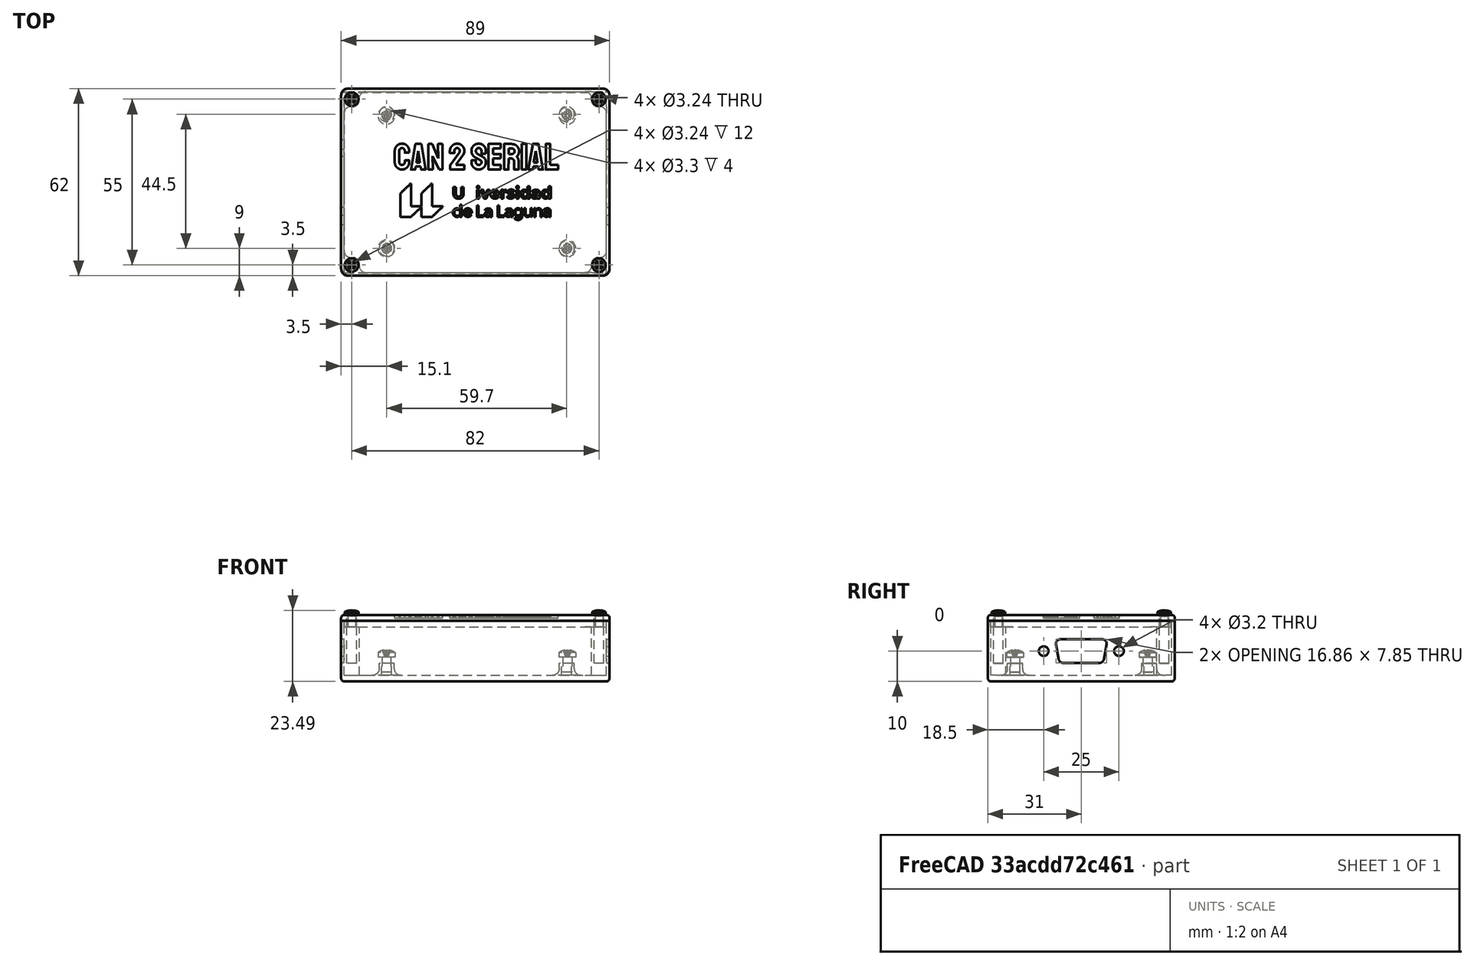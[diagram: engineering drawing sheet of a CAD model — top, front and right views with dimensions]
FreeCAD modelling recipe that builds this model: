
FCSTD DOCUMENT  (FreeCAD 0.19R24276 (Git))
Label: Carcasa_Can2Serial
License: All rights reserved
LicenseURL: http://en.wikipedia.org/wiki/All_rights_reserved
objects: Part::Feature×36, TechDraw::DrawViewDimension×25, Part::FeaturePython×22, Part::MultiFuse×9, TechDraw::DrawProjGroupItem×9, Part::Cut×7, Part::Box×5, Part::Cylinder×5, App::DocumentObjectGroup×4, Raytracing::RayFeature×4, TechDraw::DrawSVGTemplate×3, TechDraw::DrawProjGroup×3, TechDraw::DrawViewSymbol×3, TechDraw::DrawPage×3, Part::Fillet×2, Part::Extrusion×2, TechDraw::DrawViewPart×2, App::VRMLObject×1, Part::Chamfer×1, Part::Part2DObjectPython×1, +1 more types
note: 90 computed .brp shape members not serialized (recipe doc carries the construction recipe); baked Part::Feature solids carry a one-line shape summary decoded from their .brp

FEATURE [App::VRMLObject] CAN2Serial
  Placement = pos=(-195,125,7) rot=(0,0,1;0rad)
FEATURE [Part::Box] Box  label="Cubo_exterior"
  AttacherType = Attacher::AttachEngine3D
  Height = 20
  Length = 89
  Placement = pos=(-12,-44,0) rot=(0,0,1;0rad)
  Width = 62
FEATURE [Part::Feature] Solid  label="DB-9"
  Placement = pos=(76,-13,10) rot=(0.57735,-0.57735,-0.57735;2.0944rad)
  shape: bbox 16.36 x 30.9 x 12.6 mm, 153 faces (baked)
FEATURE [Part::Feature] Solid001  label="DB-9-CAN"
  Placement = pos=(-11,-13,10) rot=(0.57735,0.57735,0.57735;2.0944rad)
  shape: bbox 16.36 x 30.9 x 12.6 mm, 153 faces (baked)
FEATURE [Part::Box] Box001  label="Cubo_interior"
  AttacherType = Attacher::AttachEngine3D
  Height = 18
  Length = 87
  Placement = pos=(-11,-43,2) rot=(0,0,1;0rad)
  Width = 60
FEATURE [Part::Cut] Cut  label="Carcasa_base"
  Base = -> Box
  Tool = -> Box001
FEATURE [Part::Box] Box002  label="Cubo"
  AttacherType = Attacher::AttachEngine3D
  Height = 2
  Length = 89
  Placement = pos=(-12,-44,20) rot=(0,0,1;0rad)
  Width = 62
FEATURE [Part::Box] Box003  label="Cubo_interior001"
  AttacherType = Attacher::AttachEngine3D
  Height = 2
  Length = 86.8
  Placement = pos=(-10.9,-43.1,18) rot=(0,0,1;0rad)
  Width = 59.8
FEATURE [Part::Box] Box004  label="Cubo001"
  AttacherType = Attacher::AttachEngine3D
  Height = 16
  Length = 5
  Placement = pos=(-11,12,2) rot=(0,0,1;0rad)
  Width = 5
FEATURE [Part::Cylinder] Cylinder  label="Cilindro"
  Angle = 360
  AttacherType = Attacher::AttachEngine3D
  Height = 12
  Placement = pos=(-8.5,14.5,6) rot=(0,0,1;0rad)
  Radius = 1.62
FEATURE [Part::Cut] Cut001  label="Sujeciones"
  Base = -> Box004
  Tool = -> Cylinder
FEATURE [Part::FeaturePython] Clone  label="Sujeciones001"  # Draft clone (typed FeaturePython)
  AttacherType = Attacher::AttachEngine3D
  Fuse = false
  Objects = -> [Cut001]
  Placement = pos=(0,-55,0) rot=(0,0,1;0rad)
  Scale = (1,1,1)
FEATURE [Part::FeaturePython] Clone001  label="Sujeciones002"  # Draft clone (typed FeaturePython)
  AttacherType = Attacher::AttachEngine3D
  Fuse = false
  Objects = -> [Cut001]
  Placement = pos=(82,0,0) rot=(0,0,1;0rad)
  Scale = (1,1,1)
FEATURE [Part::FeaturePython] Clone002  label="Sujeciones003"  # Draft clone (typed FeaturePython)
  AttacherType = Attacher::AttachEngine3D
  Fuse = false
  Objects = -> [Cut001]
  Placement = pos=(82,-55,0) rot=(0,0,1;0rad)
  Scale = (1,1,1)
FEATURE [Part::Cylinder] Cylinder001  label="Cilindro001"
  Angle = 360
  AttacherType = Attacher::AttachEngine3D
  Height = 12
  Placement = pos=(-8.5,14.5,11) rot=(0,0,1;0rad)
  Radius = 1.62
FEATURE [Part::FeaturePython] Clone003  label="Cilindro002"  # Draft clone (typed FeaturePython)
  AttacherType = Attacher::AttachEngine3D
  Fuse = false
  Objects = -> [Cylinder001]
  Placement = pos=(-8.5,-40.5,11) rot=(0,0,1;0rad)
  Scale = (1,1,1)
FEATURE [Part::FeaturePython] Clone004  label="Cilindro003"  # Draft clone (typed FeaturePython)
  AttacherType = Attacher::AttachEngine3D
  Fuse = false
  Objects = -> [Clone003]
  Placement = pos=(73.5,14.5,11) rot=(0,0,1;0rad)
  Scale = (1,1,1)
FEATURE [Part::FeaturePython] Clone005  label="Cilindro004"  # Draft clone (typed FeaturePython)
  AttacherType = Attacher::AttachEngine3D
  Fuse = false
  Objects = -> [Clone004]
  Placement = pos=(73.5,-40.5,11) rot=(0,0,1;0rad)
  Scale = (1,1,1)
FEATURE [Part::MultiFuse] Fusion  label="Tapa"
  Shapes = -> [Box002,Box003]
FEATURE [Part::MultiFuse] Fusion001  label="Agujeros_tapa"
  Shapes = -> [Clone005,Clone004,Clone003,Cylinder001]
FEATURE [Part::Cut] Cut002  label="Tapa_Superior"
  Base = -> Fusion
  Tool = -> Fusion001
FEATURE [Part::MultiFuse] Fusion002  label="Carcasa_inferior"
  Shapes = -> [Cut001,Clone,Clone001,Clone002,Cut]
FEATURE [Part::Cylinder] Cylinder002  label="Cilindro005"
  Angle = 360
  AttacherType = Attacher::AttachEngine3D
  Height = 4
  Radius = 1.65
FEATURE [Part::Cylinder] Cylinder003  label="Cilindro006"
  Angle = 360
  AttacherType = Attacher::AttachEngine3D
  Height = 4
  Radius = 2.5
FEATURE [Part::Cut] Cut003  label="Soporte_PCB"
  Base = -> Cylinder003
  Placement = pos=(3.1,9.5,2) rot=(0,0,1;0rad)
  Tool = -> Cylinder002
FEATURE [Part::FeaturePython] Clone006  label="Soporte_PCB001"  # Draft clone (typed FeaturePython)
  AttacherType = Attacher::AttachEngine3D
  Fuse = false
  Objects = -> [Cut003]
  Placement = pos=(62.8,9.5,2) rot=(0,0,1;0rad)
  Scale = (1,1,1)
FEATURE [Part::FeaturePython] Clone007  label="Soporte_PCB002"  # Draft clone (typed FeaturePython)
  AttacherType = Attacher::AttachEngine3D
  Fuse = false
  Objects = -> [Clone006]
  Placement = pos=(3.1,-35,2) rot=(0,0,1;0rad)
  Scale = (1,1,1)
FEATURE [Part::FeaturePython] Clone008  label="Soporte_PCB003"  # Draft clone (typed FeaturePython)
  AttacherType = Attacher::AttachEngine3D
  Fuse = false
  Objects = -> [Clone007]
  Placement = pos=(62.8,-35,2) rot=(0,0,1;0rad)
  Scale = (1,1,1)
FEATURE [Part::MultiFuse] Fusion003  label="Soportes_PCB"
  Shapes = -> [Cut003,Clone006,Clone007,Clone008]
FEATURE [Part::MultiFuse] Fusion004  label="Carcasa_Soportes_PCB"
  Shapes = -> [Fusion002,Fusion003]
FEATURE [Part::FeaturePython] Clone009  label="DB-010"  # Draft clone (typed FeaturePython)
  AttacherType = Attacher::AttachEngine3D
  Fuse = false
  Objects = -> [Solid]
  Placement = pos=(75,-13,10) rot=(0.57735,-0.57735,-0.57735;2.0944rad)
  Scale = (1,1,1)
FEATURE [Part::FeaturePython] Clone010  label="DB-9-CAN001"  # Draft clone (typed FeaturePython)
  AttacherType = Attacher::AttachEngine3D
  Fuse = false
  Objects = -> [Solid001]
  Placement = pos=(-10,-13,10) rot=(0.57735,0.57735,0.57735;2.0944rad)
  Scale = (1,1,1)
FEATURE [Part::MultiFuse] Fusion005  label="Conectores_DB9"
  Shapes = -> [Clone010,Clone009]
FEATURE [Part::Cylinder] Cylinder004  label="Agujero_Tornillo_DB9"
  Angle = 360
  AttacherType = Attacher::AttachEngine3D
  Height = 4
  Placement = pos=(-13,-0.5,10) rot=(0,1,0;1.5708rad)
  Radius = 1.6
FEATURE [Part::FeaturePython] Clone011  label="Agujero_Tornillo_DB010"  # Draft clone (typed FeaturePython)
  AttacherType = Attacher::AttachEngine3D
  Fuse = false
  Objects = -> [Cylinder004]
  Placement = pos=(-13,-25.5,10) rot=(0,1,0;1.5708rad)
  Scale = (1,1,1)
FEATURE [Part::FeaturePython] Clone012  label="Agujero_Tornillo_DB011"  # Draft clone (typed FeaturePython)
  AttacherType = Attacher::AttachEngine3D
  Fuse = false
  Objects = -> [Clone011]
  Placement = pos=(74,-0.5,10) rot=(0,1,0;1.5708rad)
  Scale = (1,1,1)
FEATURE [Part::FeaturePython] Clone013  label="Agujero_Tornillo_DB012"  # Draft clone (typed FeaturePython)
  AttacherType = Attacher::AttachEngine3D
  Fuse = false
  Objects = -> [Clone012]
  Placement = pos=(74,-25.5,10) rot=(0,1,0;1.5708rad)
  Scale = (1,1,1)
FEATURE [Part::MultiFuse] Fusion006  label="Agujeros_tornillos_DB9"
  Shapes = -> [Clone013,Clone012,Clone011,Cylinder004]
FEATURE [Part::Cut] Cut004  label="Carcasa_huecos_DB9"
  Base = -> Fusion004
  Tool = -> Fusion005
FEATURE [Part::Cut] Cut005  label="Carcasa"
  Base = -> Cut004
  Tool = -> Fusion006
FEATURE [Part::Fillet] Fillet  label="Carcasa_Fillet"
  Base = -> Cut005
  Edges = 24 edges: [Edge2 r=2.2,Edge4 r=2.2,Edge16 r=2.2,Edge17 r=2.2,Edge18 r=2.2,Edge19 r=2.2,Edge21 r=2.2,Edge28 r=2.2,Edge40 r=2.2,Edge42 r=2.2,Edge44 r=2.2,Edge49 r=2.2,Edge54 r=2.2,Edge55 r=2.2,Edge57 r=2.2,Edge59 r=2.2,Edge137 r=2.2,Edge138 r=1,Edge139 r=2.2,Edge140 r=1,Edge141 r=2.2,Edge142 r=1,Edge143 r=2.2,Edge144 r=1]
FEATURE [Part::Fillet] Fillet001  label="Tapa_superior_fillet"
  Base = -> Cut002
  Edges = 8 edges: [Edge1 r=2.3,Edge2 r=1,Edge3 r=2.3,Edge6 r=2.3,Edge7 r=1,Edge8 r=1,Edge9 r=1,Edge15 r=2.3]
FEATURE [Part::Chamfer] Chamfer  label="Tapa_superior_chanfer"
  Base = -> Fillet001
  Edges = 4 edges r=0.4: [Edge49,Edge50,Edge51,Edge52]
FEATURE [Part::Part2DObjectPython] ShapeString  label="CAN2Serial_text"  # Draft 2D object (typed FeaturePython)
  FontFile = <userpath>/Documents/tfm_augusto/Mecanica/Carcasa_Can2Serial/Staatliches-Regular.ttf
  Placement = pos=(6.42,-8.83,22) rot=(0,0,1;0rad)
  Size = 5
  String = CAN 2 Serial
  Tracking = 0
FEATURE [Part::Extrusion] Extrude  label="CAN2Serial_extruido"
  Base = -> ShapeString
  Dir = (0,0,1)
  DirMode = 2
  FaceMakerClass = Part::FaceMakerBullseye
  LengthFwd = 1
  LengthRev = 0
  Placement = pos=(-1,0,-1) rot=(0,0,1;0rad)
  Solid = false
  Symmetric = false
FEATURE [Part::Feature] path4
  shape: bbox 3.397 x 3.83 x 2.334e-07 mm, 0 faces, 0 solids (baked)
FEATURE [Part::Feature] path8
  shape: bbox 2.841 x 2.934 x 2.334e-07 mm, 0 faces, 0 solids (baked)
FEATURE [Part::Feature] path12
  shape: bbox 0.803 x 2.903 x 2.334e-07 mm, 0 faces, 0 solids (baked)
FEATURE [Part::Feature] path12001
  shape: bbox 0.8647 x 0.9265 x 2.334e-07 mm, 0 faces, 0 solids (baked)
FEATURE [Part::Feature] path16
  shape: bbox 2.996 x 2.903 x 2.334e-07 mm, 0 faces, 0 solids (baked)
FEATURE [Part::Feature] path20
  shape: bbox 2.903 x 2.965 x 2.334e-07 mm, 0 faces, 0 solids (baked)
FEATURE [Part::Feature] path20001
  shape: bbox 1.328 x 0.6485 x 2.334e-07 mm, 0 faces, 0 solids (baked)
FEATURE [Part::Feature] path24
  shape: bbox 1.76 x 2.934 x 2.334e-07 mm, 0 faces, 0 solids (baked)
FEATURE [Part::Feature] path28
  shape: bbox 2.409 x 3.027 x 2.334e-07 mm, 0 faces, 0 solids (baked)
FEATURE [Part::Feature] path32
  shape: bbox 0.803 x 2.903 x 2.334e-07 mm, 0 faces, 0 solids (baked)
FEATURE [Part::Feature] path32001
  shape: bbox 0.8647 x 0.9265 x 2.334e-07 mm, 0 faces, 0 solids (baked)
FEATURE [Part::Feature] path36
  shape: bbox 3.088 x 4.046 x 2.334e-07 mm, 0 faces, 0 solids (baked)
FEATURE [Part::Feature] path36001
  shape: bbox 1.482 x 1.606 x 2.334e-07 mm, 0 faces, 0 solids (baked)
FEATURE [Part::Feature] path40
  shape: bbox 2.687 x 2.965 x 2.334e-07 mm, 0 faces, 0 solids (baked)
FEATURE [Part::Feature] path40001
  shape: bbox 1.143 x 0.7103 x 2.334e-07 mm, 0 faces, 0 solids (baked)
FEATURE [Part::Feature] path44
  shape: bbox 3.088 x 4.046 x 2.334e-07 mm, 0 faces, 0 solids (baked)
FEATURE [Part::Feature] path44001
  shape: bbox 1.482 x 1.606 x 2.334e-07 mm, 0 faces, 0 solids (baked)
FEATURE [Part::Feature] path48
  shape: bbox 2.903 x 4.015 x 2.334e-07 mm, 0 faces, 0 solids (baked)
FEATURE [Part::Feature] path48001
  shape: bbox 1.977 x 2.038 x 2.334e-07 mm, 0 faces, 0 solids (baked)
FEATURE [Part::Feature] path50
  shape: bbox 2.805 x 2.841 x 2.334e-07 mm, 0 faces, 0 solids (baked)
FEATURE [Part::Feature] path50001
  shape: bbox 1.884 x 0.8647 x 2.334e-07 mm, 0 faces, 0 solids (baked)
FEATURE [Part::Feature] polygon52
  shape: bbox 2.1 x 3.737 x 2.334e-07 mm, 0 faces, 0 solids (baked)
FEATURE [Part::Feature] path54
  shape: bbox 2.409 x 2.841 x 2.334e-07 mm, 0 faces, 0 solids (baked)
FEATURE [Part::Feature] path54001
  shape: bbox 1.544 x 0.9265 x 2.334e-07 mm, 0 faces, 0 solids (baked)
FEATURE [Part::Feature] polygon56
  shape: bbox 2.1 x 3.737 x 2.334e-07 mm, 0 faces, 0 solids (baked)
FEATURE [Part::Feature] path58
  shape: bbox 2.409 x 2.81 x 2.334e-07 mm, 0 faces, 0 solids (baked)
FEATURE [Part::Feature] path58001
  shape: bbox 1.544 x 0.9265 x 2.334e-07 mm, 0 faces, 0 solids (baked)
FEATURE [Part::Feature] path60
  shape: bbox 2.718 x 3.86 x 2.334e-07 mm, 0 faces, 0 solids (baked)
FEATURE [Part::Feature] path60001
  shape: bbox 1.915 x 1.946 x 2.334e-07 mm, 0 faces, 0 solids (baked)
FEATURE [Part::Feature] path62
  shape: bbox 2.563 x 2.872 x 2.334e-07 mm, 0 faces, 0 solids (baked)
FEATURE [Part::Feature] path64
  shape: bbox 2.625 x 2.841 x 2.334e-07 mm, 0 faces, 0 solids (baked)
FEATURE [Part::Feature] path66
  shape: bbox 2.378 x 2.841 x 2.334e-07 mm, 0 faces, 0 solids (baked)
FEATURE [Part::Feature] path66001
  shape: bbox 1.544 x 0.9265 x 2.334e-07 mm, 0 faces, 0 solids (baked)
FEATURE [Part::Feature] polygon72
  shape: bbox 14.08 x 10.99 x 2.334e-07 mm, 0 faces, 0 solids (baked)
FEATURE [Part::MultiFuse] Fusion007
  Placement = pos=(0,-5,22) rot=(0,0,1;0rad)
  Shapes = -> [path4,path8,path12,path12001,path16,path20,path20001,path24,path28,path32,path32001,path36,path36001,path40,path40001,path44,path44001,path48,path48001,path50,path50001,polygon52,path54,path54001,polygon56,path58,path58001,path60,path60001,path62,path64,path66,path66001,polygon72]
FEATURE [Part::Extrusion] Extrude001  label="ULL_logo"
  Base = -> Fusion007
  Dir = (0,0,1)
  DirMode = 2
  FaceMakerClass = Part::FaceMakerBullseye
  LengthFwd = 1
  LengthRev = 0
  Placement = pos=(-2,0,-1) rot=(0,0,1;0rad)
  Solid = true
  Symmetric = false
FEATURE [Part::MultiFuse] Fusion008  label="Logos"
  Shapes = -> [Extrude001,Extrude]
FEATURE [Part::Cut] Cut006  label="Tapa_con_logos"
  Base = -> Chamfer
  Tool = -> Fusion008
FEATURE [TechDraw::DrawSVGTemplate] Template
  EditableTexts = Designed_by_Name=Augusto Hernández; Drawing_number=13; FC-Date=10/05/2021; FC-SC=1:1; FC-SH=13/15; FC-Title=Carcasa de CAN2Serial; Subtitle=Carcasa de CAN2Serial. General; Weight=ND
  Height = 210
  Orientation = 1
  Width = 297
FEATURE [TechDraw::DrawProjGroupItem] ProjItem  label="Front"
  CoarseView = false
  Direction = (0,-1,0)
  Focus = 100
  HardHidden = false
  IsoCount = 0
  IsoHidden = false
  IsoVisible = false
  LockPosition = true
  Perspective = false
  Rotation = 0
  RotationVector = (1,0,0)
  ScaleType = 2
  SeamHidden = false
  SeamVisible = true
  SmoothHidden = false
  SmoothVisible = true
  Source = -> [Fillet,Cut006]
  Type = 0
  X = 0
  XDirection = (1,0,0)
  Y = 0
FEATURE [TechDraw::DrawProjGroupItem] ProjItem001  label="Left"
  CoarseView = false
  Direction = (-1,-1e-16,0)
  Focus = 100
  HardHidden = false
  IsoCount = 0
  IsoHidden = false
  IsoVisible = false
  LockPosition = true
  Perspective = false
  Rotation = 0
  RotationVector = (1,0,0)
  ScaleType = 2
  SeamHidden = false
  SeamVisible = true
  SmoothHidden = false
  SmoothVisible = true
  Source = -> [Fillet,Cut006]
  Type = 1
  X = 126.886
  XDirection = (1e-16,-1,0)
  Y = 0
FEATURE [TechDraw::DrawProjGroupItem] ProjItem002  label="Top"
  CoarseView = false
  Direction = (0,0,1)
  Focus = 100
  HardHidden = false
  IsoCount = 0
  IsoHidden = false
  IsoVisible = false
  LockPosition = true
  Perspective = false
  Rotation = 0
  RotationVector = (1,0,0)
  ScaleType = 2
  SeamHidden = false
  SeamVisible = true
  SmoothHidden = false
  SmoothVisible = true
  Source = -> [Fillet,Cut006]
  Type = 4
  X = 0
  XDirection = (1,0,0)
  Y = -76.4589
FEATURE [TechDraw::DrawProjGroup] ProjGroup
  Anchor = -> ProjItem
  AutoDistribute = true
  LockPosition = false
  ProjectionType = 0
  Rotation = 0
  ScaleType = 0
  Source = -> [Fillet,Cut006]
  Views = -> [ProjItem,ProjItem001,ProjItem002]
  X = 86.5897
  Y = 176.663
  spacingX = 15
  spacingY = 15
FEATURE [TechDraw::DrawSVGTemplate] Template001
  EditableTexts = Designed_by_Name=Augusto Hernández; Drawing_number=14; FC-Date=10/05/2021; FC-SC=1:1; FC-SH=14/15; FC-Title=Tapa de Carcasa CAN2Serial; Subtitle=Tapa de la Carcasa de CAN2Serial; Weight=ND
  Height = 210
  Orientation = 1
  Width = 297
FEATURE [TechDraw::DrawProjGroupItem] ProjItem004  label="Front001"
  CoarseView = false
  Direction = (0,0,1)
  Focus = 100
  HardHidden = false
  IsoCount = 0
  IsoHidden = false
  IsoVisible = false
  LockPosition = true
  Perspective = false
  Rotation = 0
  RotationVector = (1,0,0)
  ScaleType = 2
  SeamHidden = false
  SeamVisible = true
  SmoothHidden = false
  SmoothVisible = true
  Source = -> [Cut006]
  Type = 0
  X = 0
  XDirection = (1,0,0)
  Y = 0
FEATURE [TechDraw::DrawProjGroupItem] ProjItem005  label="Left001"
  CoarseView = false
  Direction = (-1,0,1e-16)
  Focus = 100
  HardHidden = false
  IsoCount = 0
  IsoHidden = false
  IsoVisible = false
  LockPosition = true
  Perspective = false
  Rotation = 0
  RotationVector = (1,0,0)
  ScaleType = 2
  SeamHidden = false
  SeamVisible = true
  SmoothHidden = false
  SmoothVisible = true
  Source = -> [Cut006]
  Type = 1
  X = 103.198
  XDirection = (1e-16,0,1)
  Y = 0
FEATURE [TechDraw::DrawProjGroupItem] ProjItem006  label="Top001"
  CoarseView = false
  Direction = (0,1,0)
  Focus = 100
  HardHidden = false
  IsoCount = 0
  IsoHidden = false
  IsoVisible = false
  LockPosition = true
  Perspective = false
  Rotation = 0
  RotationVector = (1,0,0)
  ScaleType = 2
  SeamHidden = false
  SeamVisible = true
  SmoothHidden = false
  SmoothVisible = true
  Source = -> [Cut006]
  Type = 4
  X = 0
  XDirection = (1,0,0)
  Y = -70.0323
FEATURE [TechDraw::DrawProjGroup] ProjGroup001
  Anchor = -> ProjItem004
  AutoDistribute = true
  LockPosition = false
  ProjectionType = 0
  Rotation = 0
  ScaleType = 0
  Source = -> [Cut006]
  Views = -> [ProjItem004,ProjItem005,ProjItem006]
  X = 95.764
  Y = 142.771
  spacingX = 15
  spacingY = 15
FEATURE [TechDraw::DrawViewDimension] Dimension
  Arbitrary = false
  ArbitraryTolerances = false
  EqualTolerance = true
  FormatSpec = %.2f
  FormatSpecOverTolerance = %+.2f
  FormatSpecUnderTolerance = %+.2f
  Inverted = false
  LockPosition = false
  MeasureType = 1
  OverTolerance = 0
  References2D = -> [ProjItem004]
  Rotation = 0
  ScaleType = 0
  TheoreticalExact = false
  Type = 2
  UnderTolerance = 0
  X = -59.9912
  Y = -3.47643
FEATURE [TechDraw::DrawViewDimension] Dimension001
  Arbitrary = false
  ArbitraryTolerances = false
  EqualTolerance = true
  FormatSpec = %.2f
  FormatSpecOverTolerance = %+.2f
  FormatSpecUnderTolerance = %+.2f
  Inverted = false
  LockPosition = false
  MeasureType = 1
  OverTolerance = 0
  References2D = -> [ProjItem004]
  Rotation = 0
  ScaleType = 0
  TheoreticalExact = false
  Type = 1
  UnderTolerance = 0
  X = -0.817985
  Y = 43.4237
FEATURE [TechDraw::DrawViewDimension] Dimension002
  Arbitrary = false
  ArbitraryTolerances = false
  EqualTolerance = true
  FormatSpec = R%.2f
  FormatSpecOverTolerance = %+.2f
  FormatSpecUnderTolerance = %+.2f
  Inverted = false
  LockPosition = false
  MeasureType = 1
  OverTolerance = 0
  References2D = -> [ProjItem004]
  Rotation = 0
  ScaleType = 0
  TheoreticalExact = false
  Type = 4
  UnderTolerance = 0
  X = 58.1063
  Y = -35.5028
FEATURE [TechDraw::DrawViewDimension] Dimension003
  Arbitrary = false
  ArbitraryTolerances = false
  EqualTolerance = true
  FormatSpec = ⌀%.2f
  FormatSpecOverTolerance = %+.2f
  FormatSpecUnderTolerance = %+.2f
  Inverted = false
  LockPosition = false
  MeasureType = 1
  OverTolerance = 0
  References2D = -> [ProjItem004]
  Rotation = 0
  ScaleType = 0
  TheoreticalExact = false
  Type = 5
  UnderTolerance = 0
  X = -33.136
  Y = -17.3964
FEATURE [TechDraw::DrawViewDimension] Dimension004
  Arbitrary = false
  ArbitraryTolerances = false
  EqualTolerance = true
  FormatSpec = %.2f
  FormatSpecOverTolerance = %+.2f
  FormatSpecUnderTolerance = %+.2f
  Inverted = false
  LockPosition = false
  MeasureType = 1
  OverTolerance = 0
  References2D = -> [ProjItem004]
  Rotation = 0
  ScaleType = 0
  TheoreticalExact = false
  Type = 1
  UnderTolerance = 0
  X = 29.9312
  Y = 23.3321
FEATURE [TechDraw::DrawViewDimension] Dimension005
  Arbitrary = false
  ArbitraryTolerances = false
  EqualTolerance = true
  FormatSpec = %.2f
  FormatSpecOverTolerance = %+.2f
  FormatSpecUnderTolerance = %+.2f
  Inverted = false
  LockPosition = false
  MeasureType = 1
  OverTolerance = 0
  References2D = -> [ProjItem005]
  Rotation = 0
  ScaleType = 0
  TheoreticalExact = false
  Type = 1
  UnderTolerance = 0
  X = -14.0312
  Y = 41.547
FEATURE [TechDraw::DrawViewDimension] Dimension006
  Arbitrary = false
  ArbitraryTolerances = false
  EqualTolerance = true
  FormatSpec = %.2f
  FormatSpecOverTolerance = %+.2f
  FormatSpecUnderTolerance = %+.2f
  Inverted = false
  LockPosition = false
  MeasureType = 1
  OverTolerance = 0
  References2D = -> [ProjItem005]
  Rotation = 0
  ScaleType = 0
  TheoreticalExact = false
  Type = 2
  UnderTolerance = 0
  X = -10.5345
  Y = -0.740158
FEATURE [TechDraw::DrawViewDimension] Dimension007
  Arbitrary = false
  ArbitraryTolerances = false
  EqualTolerance = true
  FormatSpec = %.2f
  FormatSpecOverTolerance = %+.2f
  FormatSpecUnderTolerance = %+.2f
  Inverted = false
  LockPosition = false
  MeasureType = 1
  OverTolerance = 0
  References2D = -> [ProjItem005]
  Rotation = 0
  ScaleType = 0
  TheoreticalExact = false
  Type = 1
  UnderTolerance = 0
  X = 18.179
  Y = -31.2999
FEATURE [TechDraw::DrawSVGTemplate] Template002
  EditableTexts = Designed_by_Name=Augusto Hernández; Drawing_number=15; FC-Date=10/05/2021; FC-SC=1:1; FC-SH=15/15; FC-Title=Base Carcasa CAN2Serial; Subtitle=Base para la Carcasa de CAN2Serial; Weight=ND
  Height = 210
  Orientation = 1
  Width = 297
FEATURE [TechDraw::DrawProjGroupItem] ProjItem007  label="Front002"
  CoarseView = false
  Direction = (0,0,1)
  Focus = 100
  HardHidden = true
  IsoCount = 0
  IsoHidden = false
  IsoVisible = false
  LockPosition = true
  Perspective = false
  Rotation = 0
  RotationVector = (1,0,0)
  ScaleType = 2
  SeamHidden = false
  SeamVisible = true
  SmoothHidden = false
  SmoothVisible = true
  Source = -> [Fillet]
  Type = 0
  X = 0
  XDirection = (1,0,0)
  Y = 0
FEATURE [TechDraw::DrawProjGroupItem] ProjItem008  label="Left002"
  CoarseView = false
  Direction = (-1,0,1e-16)
  Focus = 100
  HardHidden = false
  IsoCount = 0
  IsoHidden = false
  IsoVisible = false
  LockPosition = true
  Perspective = false
  Rotation = 0
  RotationVector = (1,0,0)
  ScaleType = 2
  SeamHidden = false
  SeamVisible = true
  SmoothHidden = false
  SmoothVisible = true
  Source = -> [Fillet]
  Type = 1
  X = 106.25
  XDirection = (1e-16,0,1)
  Y = 0
FEATURE [TechDraw::DrawProjGroupItem] ProjItem009  label="Top002"
  CoarseView = false
  Direction = (0,1,0)
  Focus = 100
  HardHidden = true
  IsoCount = 0
  IsoHidden = false
  IsoVisible = false
  LockPosition = true
  Perspective = false
  Rotation = 0
  RotationVector = (1,0,0)
  ScaleType = 2
  SeamHidden = false
  SeamVisible = true
  SmoothHidden = false
  SmoothVisible = true
  Source = -> [Fillet]
  Type = 4
  X = 0
  XDirection = (1,0,0)
  Y = -68.7232
FEATURE [TechDraw::DrawProjGroup] ProjGroup002
  Anchor = -> ProjItem007
  AutoDistribute = true
  LockPosition = false
  ProjectionType = 0
  Rotation = 0
  ScaleType = 0
  Source = -> [Fillet]
  Views = -> [ProjItem007,ProjItem008,ProjItem009]
  X = 95.848
  Y = 148.464
  spacingX = 15
  spacingY = 15
FEATURE [TechDraw::DrawViewDimension] Dimension008
  Arbitrary = false
  ArbitraryTolerances = false
  EqualTolerance = true
  FormatSpec = %.2f
  FormatSpecOverTolerance = %+.2f
  FormatSpecUnderTolerance = %+.2f
  Inverted = false
  LockPosition = false
  MeasureType = 1
  OverTolerance = 0
  References2D = -> [ProjItem007]
  Rotation = 0
  ScaleType = 0
  TheoreticalExact = false
  Type = 1
  UnderTolerance = 0
  X = 0.108032
  Y = 43.3959
FEATURE [TechDraw::DrawViewDimension] Dimension009
  Arbitrary = false
  ArbitraryTolerances = false
  EqualTolerance = true
  FormatSpec = ⌀%.2f
  FormatSpecOverTolerance = %+.2f
  FormatSpecUnderTolerance = %+.2f
  Inverted = false
  LockPosition = false
  MeasureType = 1
  OverTolerance = 0
  References2D = -> [ProjItem007]
  Rotation = 0
  ScaleType = 0
  TheoreticalExact = false
  Type = 5
  UnderTolerance = 0
  X = -54.664
  Y = 42.5645
FEATURE [TechDraw::DrawViewDimension] Dimension010
  Arbitrary = false
  ArbitraryTolerances = false
  EqualTolerance = true
  FormatSpec = R%.2f
  FormatSpecOverTolerance = %+.2f
  FormatSpecUnderTolerance = %+.2f
  Inverted = false
  LockPosition = false
  MeasureType = 1
  OverTolerance = 0
  References2D = -> [ProjItem007]
  Rotation = 0
  ScaleType = 0
  TheoreticalExact = false
  Type = 4
  UnderTolerance = 0
  X = 47.5339
  Y = 44.7251
FEATURE [TechDraw::DrawViewDimension] Dimension012
  Arbitrary = false
  ArbitraryTolerances = false
  EqualTolerance = true
  FormatSpec = ⌀%.2f
  FormatSpecOverTolerance = %+.2f
  FormatSpecUnderTolerance = %+.2f
  Inverted = false
  LockPosition = false
  MeasureType = 1
  OverTolerance = 0
  References2D = -> [ProjItem007]
  Rotation = 0
  ScaleType = 0
  TheoreticalExact = false
  Type = 5
  UnderTolerance = 0
  X = -18.4204
  Y = -8.25165
FEATURE [TechDraw::DrawViewDimension] Dimension013
  Arbitrary = false
  ArbitraryTolerances = false
  EqualTolerance = true
  FormatSpec = ⌀%.2f
  FormatSpecOverTolerance = %+.2f
  FormatSpecUnderTolerance = %+.2f
  Inverted = false
  LockPosition = false
  MeasureType = 1
  OverTolerance = 0
  References2D = -> [ProjItem007]
  Rotation = 0
  ScaleType = 0
  TheoreticalExact = false
  Type = 5
  UnderTolerance = 0
  X = 19.6671
  Y = -8.92632
FEATURE [TechDraw::DrawViewDimension] Dimension014
  Arbitrary = false
  ArbitraryTolerances = false
  EqualTolerance = true
  FormatSpec = %.2f
  FormatSpecOverTolerance = %+.2f
  FormatSpecUnderTolerance = %+.2f
  Inverted = false
  LockPosition = false
  MeasureType = 1
  OverTolerance = 0
  References2D = -> [ProjItem007]
  Rotation = 0
  ScaleType = 0
  TheoreticalExact = false
  Type = 1
  UnderTolerance = 0
  X = 54.2725
  Y = -34.1105
FEATURE [TechDraw::DrawViewDimension] Dimension015
  Arbitrary = false
  ArbitraryTolerances = false
  EqualTolerance = true
  FormatSpec = %.2f
  FormatSpecOverTolerance = %+.2f
  FormatSpecUnderTolerance = %+.2f
  Inverted = false
  LockPosition = false
  MeasureType = 1
  OverTolerance = 0
  References2D = -> [ProjItem007]
  Rotation = 0
  ScaleType = 0
  TheoreticalExact = false
  Type = 1
  UnderTolerance = 0
  X = 54.3303
  Y = -9.63716
FEATURE [TechDraw::DrawViewDimension] Dimension016
  Arbitrary = false
  ArbitraryTolerances = false
  EqualTolerance = true
  FormatSpec = %.2f
  FormatSpecOverTolerance = %+.2f
  FormatSpecUnderTolerance = %+.2f
  Inverted = false
  LockPosition = false
  MeasureType = 1
  OverTolerance = 0
  References2D = -> [ProjItem007]
  Rotation = 0
  ScaleType = 0
  TheoreticalExact = false
  Type = 1
  UnderTolerance = 0
  X = -51.8874
  Y = -33.879
FEATURE [TechDraw::DrawViewDimension] Dimension017
  Arbitrary = false
  ArbitraryTolerances = false
  EqualTolerance = true
  FormatSpec = %.2f
  FormatSpecOverTolerance = %+.2f
  FormatSpecUnderTolerance = %+.2f
  Inverted = false
  LockPosition = false
  MeasureType = 1
  OverTolerance = 0
  References2D = -> [ProjItem009]
  Rotation = 0
  ScaleType = 0
  TheoreticalExact = false
  Type = 2
  UnderTolerance = 0
  X = 53.9563
  Y = 1.43147
FEATURE [TechDraw::DrawViewDimension] Dimension019
  Arbitrary = false
  ArbitraryTolerances = false
  EqualTolerance = true
  FormatSpec = %.2f
  FormatSpecOverTolerance = %+.2f
  FormatSpecUnderTolerance = %+.2f
  Inverted = false
  LockPosition = false
  MeasureType = 1
  OverTolerance = 0
  References2D = -> [ProjItem009]
  Rotation = 0
  ScaleType = 0
  TheoreticalExact = false
  Type = 1
  UnderTolerance = 0
  X = 0
  Y = -12.9122
FEATURE [TechDraw::DrawViewDimension] Dimension020
  Arbitrary = false
  ArbitraryTolerances = false
  EqualTolerance = true
  FormatSpec = ⌀%.2f
  FormatSpecOverTolerance = %+.2f
  FormatSpecUnderTolerance = %+.2f
  Inverted = false
  LockPosition = false
  MeasureType = 1
  OverTolerance = 0
  References2D = -> [ProjItem008]
  Rotation = 0
  ScaleType = 0
  TheoreticalExact = false
  Type = 5
  UnderTolerance = 0
  X = 16.6009
  Y = 23.9151
FEATURE [TechDraw::DrawViewDimension] Dimension021
  Arbitrary = false
  ArbitraryTolerances = false
  EqualTolerance = true
  FormatSpec = %.2f
  FormatSpecOverTolerance = %+.2f
  FormatSpecUnderTolerance = %+.2f
  Inverted = false
  LockPosition = false
  MeasureType = 1
  OverTolerance = 0
  References2D = -> [ProjItem008]
  Rotation = 0
  ScaleType = 0
  TheoreticalExact = false
  Type = 2
  UnderTolerance = 0
  X = -23.6267
  Y = -20.0242
FEATURE [TechDraw::DrawViewDimension] Dimension022
  Arbitrary = false
  ArbitraryTolerances = false
  EqualTolerance = true
  FormatSpec = %.2f
  FormatSpecOverTolerance = %+.2f
  FormatSpecUnderTolerance = %+.2f
  Inverted = false
  LockPosition = false
  MeasureType = 1
  OverTolerance = 0
  References2D = -> [ProjItem008]
  Rotation = 0
  ScaleType = 0
  TheoreticalExact = false
  Type = 1
  UnderTolerance = 0
  X = 21.5318
  Y = 3.02023
FEATURE [TechDraw::DrawViewDimension] Dimension023
  Arbitrary = false
  ArbitraryTolerances = false
  EqualTolerance = true
  FormatSpec = %.2f
  FormatSpecOverTolerance = %+.2f
  FormatSpecUnderTolerance = %+.2f
  Inverted = false
  LockPosition = false
  MeasureType = 1
  OverTolerance = 0
  References2D = -> [ProjItem008]
  Rotation = 0
  ScaleType = 0
  TheoreticalExact = false
  Type = 1
  UnderTolerance = 0
  X = 20.9634
  Y = 10.56
FEATURE [TechDraw::DrawViewDimension] Dimension024
  Arbitrary = false
  ArbitraryTolerances = false
  EqualTolerance = true
  FormatSpec = %.2f
  FormatSpecOverTolerance = %+.2f
  FormatSpecUnderTolerance = %+.2f
  Inverted = false
  LockPosition = false
  MeasureType = 1
  OverTolerance = 0
  References2D = -> [ProjItem009]
  Rotation = 0
  ScaleType = 0
  TheoreticalExact = false
  Type = 2
  UnderTolerance = 0
  X = -23.7672
  Y = 21.1904
FEATURE [TechDraw::DrawViewDimension] Dimension025
  Arbitrary = false
  ArbitraryTolerances = false
  EqualTolerance = true
  FormatSpec = %.2f
  FormatSpecOverTolerance = %+.2f
  FormatSpecUnderTolerance = %+.2f
  Inverted = false
  LockPosition = false
  MeasureType = 1
  OverTolerance = 0
  References2D = -> [ProjItem009]
  Rotation = 0
  ScaleType = 0
  TheoreticalExact = false
  Type = 2
  UnderTolerance = 0
  X = -56.5528
  Y = -15.9933
FEATURE [TechDraw::DrawViewDimension] Dimension026
  Arbitrary = false
  ArbitraryTolerances = false
  EqualTolerance = true
  FormatSpec = %.2f
  FormatSpecOverTolerance = %+.2f
  FormatSpecUnderTolerance = %+.2f
  Inverted = false
  LockPosition = false
  MeasureType = 1
  OverTolerance = 0
  References2D = -> [ProjItem009]
  Rotation = 0
  ScaleType = 0
  TheoreticalExact = false
  Type = 2
  UnderTolerance = 0
  X = -11.6878
  Y = 1.42011
FEATURE [TechDraw::DrawViewPart] View
  CoarseView = false
  Direction = (0.577,0.577,0.577)
  Focus = 100
  HardHidden = false
  IsoCount = 0
  IsoHidden = false
  IsoVisible = false
  LockPosition = true
  Perspective = false
  Rotation = 0
  Scale = 0.5
  ScaleType = 0
  SeamHidden = false
  SeamVisible = true
  SmoothHidden = false
  SmoothVisible = true
  Source = -> [Fillet]
  X = 217.113
  XDirection = (-0.707,0.707,0)
  Y = 85.5647
FEATURE [App::DocumentObjectGroup] Group001  label="Modelos_3D"
  Group = -> [Solid001,Solid,CAN2Serial]
FEATURE [App::DocumentObjectGroup] Group002  label="Carcasa_caja"
  Group = -> [Cut006,Fillet]
FEATURE [Part::FeaturePython] Screw001  label="M3x5-Screw001"  # Fasteners workbench fastener (typed FeaturePython)
  Placement = pos=(63,9,8) rot=(0,0,1;0rad)
  diameter = 4
  invert = false
  length = 1
  lengthCustom = 5
  matchOuter = false
  offset = 0
  thread = false
  type = 34
FEATURE [Part::FeaturePython] Screw002  label="M3x5-Screw002"  # Fasteners workbench fastener (typed FeaturePython)
  Placement = pos=(3,-35,8) rot=(0,0,1;0rad)
  diameter = 4
  invert = false
  length = 1
  lengthCustom = 5
  matchOuter = false
  offset = 0
  thread = false
  type = 34
FEATURE [Part::FeaturePython] Screw  label="M3x5-Screw"  # Fasteners workbench fastener (typed FeaturePython)
  Placement = pos=(63,-35,8) rot=(0,0,1;0rad)
  diameter = 4
  invert = false
  length = 1
  lengthCustom = 5
  matchOuter = false
  offset = 0
  thread = false
  type = 34
FEATURE [Part::FeaturePython] Screw003  label="M3x5-Screw003"  # Fasteners workbench fastener (typed FeaturePython)
  Placement = pos=(3,9,8) rot=(0,0,1;0rad)
  diameter = 4
  invert = false
  length = 1
  lengthCustom = 5
  matchOuter = false
  offset = 0
  thread = false
  type = 34
FEATURE [Part::FeaturePython] Screw004  label="M2.5x5-Screw"  # Fasteners workbench fastener (typed FeaturePython)
  Placement = pos=(-8.5,14.5,23) rot=(0,0,1;0rad)
  diameter = 3
  invert = false
  length = 2
  lengthCustom = 5
  matchOuter = false
  offset = 0
  thread = false
  type = 36
FEATURE [Part::FeaturePython] Screw005  label="M2.5x5-Screw001"  # Fasteners workbench fastener (typed FeaturePython)
  Placement = pos=(73.5,14.5,23) rot=(0,0,1;0rad)
  diameter = 3
  invert = false
  length = 2
  lengthCustom = 5
  matchOuter = false
  offset = 0
  thread = false
  type = 36
FEATURE [Part::FeaturePython] Screw006  label="M2.5x5-Screw002"  # Fasteners workbench fastener (typed FeaturePython)
  Placement = pos=(73.5,-40.5,23) rot=(0,0,1;0rad)
  diameter = 3
  invert = false
  length = 2
  lengthCustom = 5
  matchOuter = false
  offset = 0
  thread = false
  type = 36
FEATURE [Part::FeaturePython] Screw007  label="M2.5x5-Screw003"  # Fasteners workbench fastener (typed FeaturePython)
  Placement = pos=(-8.5,-40.5,23) rot=(0,0,1;0rad)
  diameter = 3
  invert = false
  length = 2
  lengthCustom = 5
  matchOuter = false
  offset = 0
  thread = false
  type = 36
FEATURE [App::DocumentObjectGroup] Group003  label="Tornillos"
  Group = -> [Screw003,Screw002,Screw,Screw001,Screw004,Screw005,Screw006,Screw007]
FEATURE [Raytracing::RayFeature] Cut006_View
  Result = <blob: 527231 chars omitted>
  Source = -> Cut006
  Transparency = 0
FEATURE [Raytracing::RayFeature] Fillet_View
  Result = <blob: 288232 chars omitted>
  Source = -> Fillet
  Transparency = 0
FEATURE [Raytracing::RayFeature] Solid_View
  Result = <blob: 369278 chars omitted>
  Source = -> Solid
  Transparency = 0
FEATURE [Raytracing::RayFeature] Solid001_View
  Result = <blob: 373823 chars omitted>
  Source = -> Solid001
  Transparency = 0
FEATURE [Raytracing::RayProject] PovProject001
  Camera = // declares position and view direction\n\n// Generated by FreeCAD (http://www.freecadweb.org/)\n#declare cam_location =  <-53.8051,98.558,-106.888>;\n#declare cam_look_at  = <6.09959,38.6534,-46.9829>;\n#declare cam_sky      = <0.408248,0.816497,0.408248>;\n#declare cam_angle    = 45; \ncamera {\n  location  cam_location\n  look_at   cam_look_at\n  sky       cam_sky\n  angle     cam_angle \n  right x*1920/1080\n}
  Group = -> [Cut006_View,Fillet_View,Solid_View,Solid001_View]
  Template = <path>
FEATURE [TechDraw::DrawViewSymbol] Symbol
  LockPosition = false
  Rotation = 0
  ScaleType = 2
  Symbol = <blob: 50210 chars omitted>
  X = 213.904
  Y = 33.9517
FEATURE [TechDraw::DrawViewSymbol] Symbol001
  LockPosition = false
  Rotation = 0
  ScaleType = 2
  Symbol = <blob: 50523 chars omitted>
  X = 213.724
  Y = 34.3412
FEATURE [TechDraw::DrawPage] Page001  label="Plano_tapa"
  KeepUpdated = true
  NextBalloonIndex = 1
  ProjectionType = 0
  Template = -> Template001
  Views = -> [ProjGroup001,Dimension,Dimension001,Dimension002,Dimension003,Dimension004,Dimension005,Dimension006,Dimension007,Symbol001]
FEATURE [TechDraw::DrawViewSymbol] Symbol002
  LockPosition = false
  Rotation = 0
  ScaleType = 2
  Symbol = <blob: 50523 chars omitted>
  X = 213.971
  Y = 33.8471
FEATURE [TechDraw::DrawPage] Page002  label="Plano_base"
  KeepUpdated = true
  NextBalloonIndex = 1
  ProjectionType = 0
  Template = -> Template002
  Views = -> [ProjGroup002,Dimension008,Dimension009,Dimension010,Dimension012,Dimension013,Dimension014,Dimension015,Dimension016,Dimension017,Dimension019,Dimension020,Dimension021,Dimension022,Dimension023,Dimension024,Dimension025,Dimension026,View,Symbol002]
FEATURE [TechDraw::DrawViewPart] View001
  CoarseView = false
  Direction = (-0.577,-0.577,0.577)
  Focus = 100
  HardHidden = false
  IsoCount = 0
  IsoHidden = false
  IsoVisible = false
  LockPosition = true
  Perspective = false
  Rotation = 0
  Scale = 0.8
  ScaleType = 0
  SeamHidden = false
  SeamVisible = true
  SmoothHidden = false
  SmoothVisible = true
  Source = -> [Cut006,Fillet,Solid,Solid001]
  X = 216.441
  XDirection = (0.707,-0.707,0)
  Y = 101.541
FEATURE [TechDraw::DrawPage] Page  label="Plano_general"
  KeepUpdated = true
  NextBalloonIndex = 1
  ProjectionType = 0
  Template = -> Template
  Views = -> [ProjGroup,Symbol,View001]
FEATURE [App::DocumentObjectGroup] Group  label="Planos"
  Group = -> [Page,Page001,Page002]
note: 1 file-system path scrubbed to <path> (originals preserved in the JSON sidecar)
